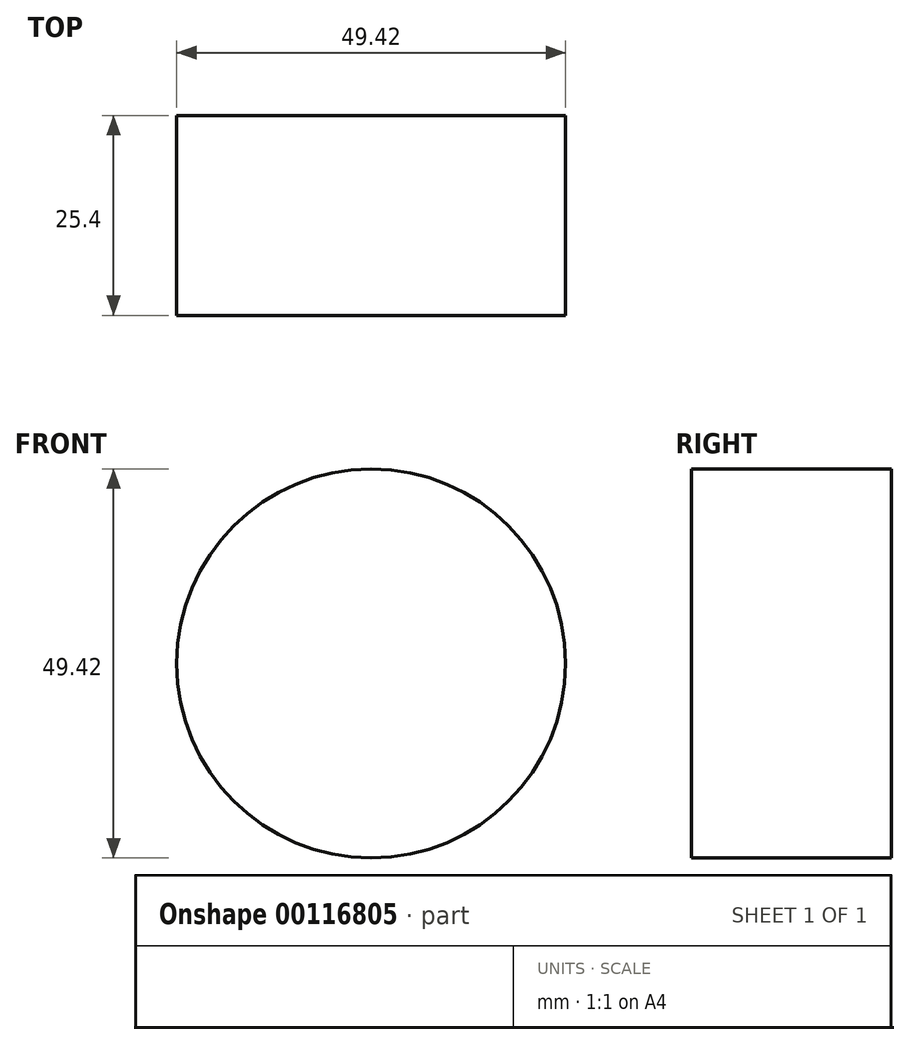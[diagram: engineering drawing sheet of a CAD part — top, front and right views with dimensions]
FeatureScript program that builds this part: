
annotation { "Feature Type Name" : "Feature", "Feature Type Description" : "" }
export const myFeature = defineFeature(function(context is Context, id is Id, definition is map)
    precondition{}
    {
        {
            var Q0;
            Q0=qCreatedBy(makeId("Front.planeOp"),FACE);
            var sketch = newSketch(context, id + "F0", { "sketchPlane" : qUnion([Q0])});
            skCircle(sketch, "E0", {"center": v(0, 0) * mm, "radius": 24.7 * mm});
            skSolve(sketch);
        }
        {
            var Q0;
            Q0 = qSketchRegion(id + "F0", true);
            extrude(context, id + "F1", {"entities" : qUnion([Q0]), "depth" : 25.4 * mm});
        }
    });
